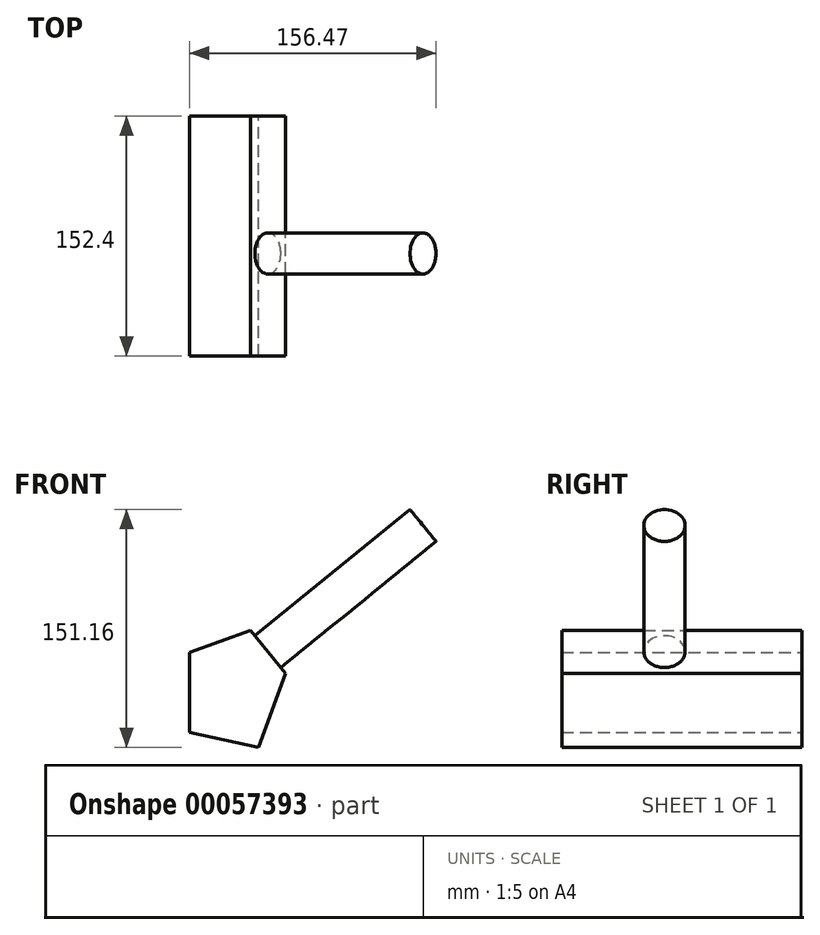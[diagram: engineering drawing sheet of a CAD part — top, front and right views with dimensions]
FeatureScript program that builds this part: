
annotation { "Feature Type Name" : "Feature", "Feature Type Description" : "" }
export const myFeature = defineFeature(function(context is Context, id is Id, definition is map)
    precondition{}
    {
        {
            var Q0;
            Q0=qCreatedBy(makeId("Front.planeOp"),FACE);
            var sketch = newSketch(context, id + "F0", { "sketchPlane" : qUnion([Q0])});
            skLineSegment(sketch, "E0", {"start": v(-28.62, -27.46) * mm, "end": v(-28.62, 23.31) * mm});
            skLineSegment(sketch, "E1", {"start": v(-28.62, 23.31) * mm, "end": v(10.16, 37.16) * mm});
            skLineSegment(sketch, "E2", {"start": v(10.16, 37.16) * mm, "end": v(32.31, 9.92) * mm});
            skLineSegment(sketch, "E3", {"start": v(32.31, 9.92) * mm, "end": v(15.23, -37.16) * mm});
            skLineSegment(sketch, "E4", {"start": v(15.23, -37.16) * mm, "end": v(-28.62, -27.46) * mm});
            skSolve(sketch);
        }
        {
            var Q0;
            Q0 = qSketchRegion(id + "F0", true);
            extrude(context, id + "F1", {"entities" : qUnion([Q0]), "depth" : 152.4 * mm});
        }
        {
            var Q0;
            Q0=makeQuery(id+"F1.opExtrude","SWEPT_FACE",FACE,{"disambiguationData":[OSD([sQuery(id+"F0.wireOp",EDGE,"E2")])]});
            var sketch = newSketch(context, id + "F2", { "sketchPlane" : qUnion([Q0])});
            skCircle(sketch, "E5", {"center": v(-87.28, 5.1) * mm, "radius": 13.06 * mm});
            skSolve(sketch);
        }
        {
            var Q0;
            Q0 = qSketchRegion(id + "F2", true);
            extrude(context, id + "F3", {"entities" : qUnion([Q0]), "operationType" : NewBodyOperationType.ADD, "depth" : 127 * mm});
        }
    });
